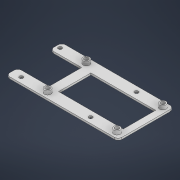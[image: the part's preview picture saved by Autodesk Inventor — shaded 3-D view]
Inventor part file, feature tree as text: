
AUTODESK INVENTOR PART (.ipt)
format: ipt  version: 2021 (Build 250183000, 183)  size: 352,256 bytes
history: native  units: mm
features: extrude x6, sketch x5, fillet x2
ambient origin geometry x8: Origin, YZ Plane, XZ Plane, XY Plane, X Axis, Y Axis, Z Axis, Center Point
bodies: Volumenkörper1 (feature_tree)
feature tree (13):
  extrude  "Extrusion1"  Depth=60.0mm
  sketch  "Skizze2"  dims[d2=2.0mm d3=0.0mm d4=4.5mm]
  extrude  "Extrusion2"  Depth=2.0mm
  extrude  "Extrusion3"  Depth=15.24mm
  extrude  "Extrusion4"  Depth=24.13mm
  extrude  "Extrusion5"  Depth=4.0mm
  extrude  "Extrusion6"  Depth=4.0mm
  fillet  "Rundung1"  Radius=82.55mm
  fillet  "Rundung2"  Radius=4.5mm
  sketch  "Skizze1"  dims[d0=130.0mm d1=60.0mm]
  sketch  "Skizze3"  dims[d5=24.13mm d6=15.24mm]
  sketch  "Skizze4"  dims[d7=4.5mm d8=24.13mm]
  sketch  "Skizze5"  dims[d9=13.97mm d10=4.5mm d11=24.13mm d12=82.55mm d13=4.5mm d14=24.13mm d15=74.93mm d16=4.0mm d17=4.0mm d18=4.0mm d19=82.55mm d20=4.0mm d21=74.93mm d22=24.13mm d23=24.13mm d24=11.392317mm d25=5.042317mm d26=24.13mm d27=24.13mm d28=2.0mm d29=0.0mm d30=35.0mm d31=35.0mm d32=2.0mm d33=0.0mm d34=1.0mm d35=0.0mm d36=70.0mm d37=35.0mm d38=15.0mm d39=8.0mm d40=0.0mm d41=7.0mm d42=7.0mm d43=7.0mm d44=7.0mm d45=4.0mm d46=0.0mm d47=4.0mm d48=4.0mm]
